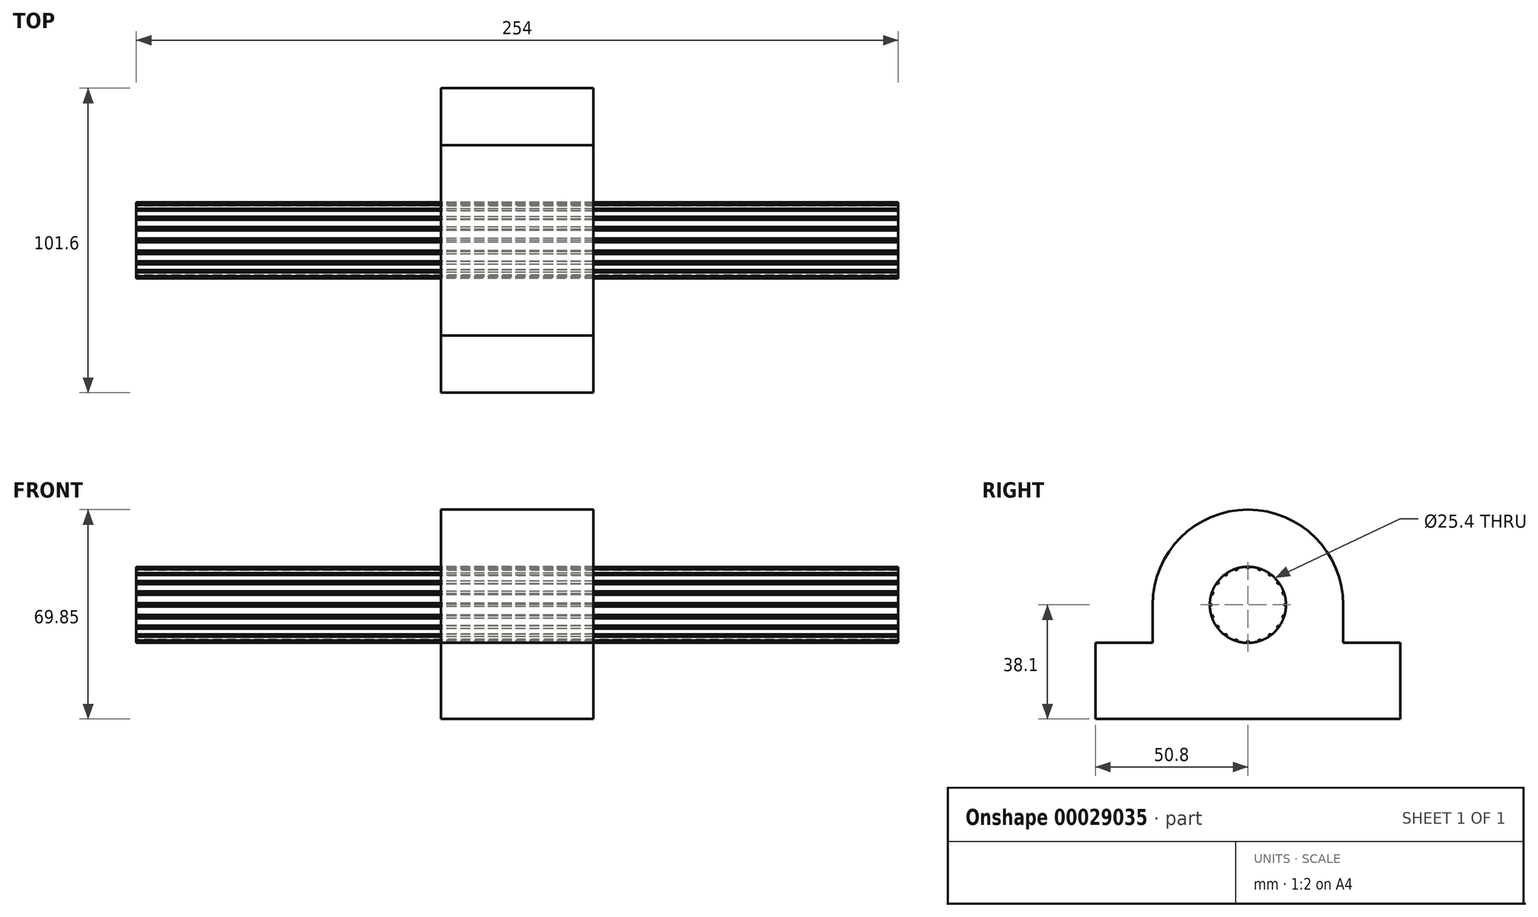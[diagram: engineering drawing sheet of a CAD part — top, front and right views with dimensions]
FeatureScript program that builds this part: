
annotation { "Feature Type Name" : "Feature", "Feature Type Description" : "" }
export const myFeature = defineFeature(function(context is Context, id is Id, definition is map)
    precondition{}
    {
        {
            var Q0;
            Q0=qCreatedBy(makeId("Right.planeOp"),FACE);
            var sketch = newSketch(context, id + "F0", { "sketchPlane" : qUnion([Q0])});
            skArc(sketch, "E0", {"start": v(-0.62, 12.68) * mm, "mid": v(-1.99, 12.54) * mm, "end": v(-3.33, 12.26) * mm});
            skLineSegment(sketch, "E1", {"start": v(-0.62, 12.68) * mm, "end": v(0, 12.06) * mm});
            skLineSegment(sketch, "E2", {"start": v(0, 12.06) * mm, "end": v(0.62, 12.68) * mm});
            skCircle(sketch, "E3", {"center": v(0, 0) * mm, "radius": 12.07 * mm, "construction": true});
            skLineSegment(sketch, "E4.1.0", {"start": v(-4.5, 11.87) * mm, "end": v(-3.73, 11.47) * mm});
            skLineSegment(sketch, "E4.1.1", {"start": v(-3.73, 11.47) * mm, "end": v(-3.33, 12.26) * mm});
            skLineSegment(sketch, "E4.2.0", {"start": v(-7.96, 9.9) * mm, "end": v(-7.1, 9.76) * mm});
            skLineSegment(sketch, "E4.2.1", {"start": v(-7.1, 9.76) * mm, "end": v(-6.95, 10.63) * mm});
            skLineSegment(sketch, "E4.3.0", {"start": v(-10.63, 6.95) * mm, "end": v(-9.76, 7.1) * mm});
            skLineSegment(sketch, "E4.3.1", {"start": v(-9.76, 7.1) * mm, "end": v(-9.9, 7.96) * mm});
            skLineSegment(sketch, "E4.4.0", {"start": v(-12.26, 3.33) * mm, "end": v(-11.47, 3.73) * mm});
            skLineSegment(sketch, "E4.4.1", {"start": v(-11.47, 3.73) * mm, "end": v(-11.87, 4.5) * mm});
            skLineSegment(sketch, "E4.5.0", {"start": v(-12.68, -0.62) * mm, "end": v(-12.06, 0) * mm});
            skLineSegment(sketch, "E4.5.1", {"start": v(-12.06, 0) * mm, "end": v(-12.68, 0.62) * mm});
            skLineSegment(sketch, "E4.6.0", {"start": v(-11.87, -4.5) * mm, "end": v(-11.47, -3.73) * mm});
            skLineSegment(sketch, "E4.6.1", {"start": v(-11.47, -3.73) * mm, "end": v(-12.26, -3.33) * mm});
            skLineSegment(sketch, "E4.7.0", {"start": v(-9.9, -7.96) * mm, "end": v(-9.76, -7.1) * mm});
            skLineSegment(sketch, "E4.7.1", {"start": v(-9.76, -7.1) * mm, "end": v(-10.63, -6.95) * mm});
            skLineSegment(sketch, "E4.8.0", {"start": v(-6.95, -10.63) * mm, "end": v(-7.1, -9.76) * mm});
            skLineSegment(sketch, "E4.8.1", {"start": v(-7.1, -9.76) * mm, "end": v(-7.96, -9.9) * mm});
            skLineSegment(sketch, "E4.9.0", {"start": v(-3.33, -12.26) * mm, "end": v(-3.73, -11.47) * mm});
            skLineSegment(sketch, "E4.9.1", {"start": v(-3.73, -11.47) * mm, "end": v(-4.5, -11.87) * mm});
            skLineSegment(sketch, "E4.10.0", {"start": v(0.62, -12.68) * mm, "end": v(0, -12.06) * mm});
            skLineSegment(sketch, "E4.10.1", {"start": v(0, -12.06) * mm, "end": v(-0.62, -12.68) * mm});
            skLineSegment(sketch, "E4.11.0", {"start": v(4.5, -11.87) * mm, "end": v(3.73, -11.47) * mm});
            skLineSegment(sketch, "E4.11.1", {"start": v(3.73, -11.47) * mm, "end": v(3.33, -12.26) * mm});
            skLineSegment(sketch, "E4.12.0", {"start": v(7.96, -9.9) * mm, "end": v(7.1, -9.76) * mm});
            skLineSegment(sketch, "E4.12.1", {"start": v(7.1, -9.76) * mm, "end": v(6.95, -10.63) * mm});
            skLineSegment(sketch, "E4.13.0", {"start": v(10.63, -6.95) * mm, "end": v(9.76, -7.1) * mm});
            skLineSegment(sketch, "E4.13.1", {"start": v(9.76, -7.1) * mm, "end": v(9.9, -7.96) * mm});
            skLineSegment(sketch, "E4.14.0", {"start": v(12.26, -3.33) * mm, "end": v(11.47, -3.73) * mm});
            skLineSegment(sketch, "E4.14.1", {"start": v(11.47, -3.73) * mm, "end": v(11.87, -4.5) * mm});
            skLineSegment(sketch, "E4.15.0", {"start": v(12.68, 0.62) * mm, "end": v(12.06, 0) * mm});
            skLineSegment(sketch, "E4.15.1", {"start": v(12.06, 0) * mm, "end": v(12.68, -0.62) * mm});
            skLineSegment(sketch, "E4.16.0", {"start": v(11.87, 4.5) * mm, "end": v(11.47, 3.73) * mm});
            skLineSegment(sketch, "E4.16.1", {"start": v(11.47, 3.73) * mm, "end": v(12.26, 3.33) * mm});
            skLineSegment(sketch, "E4.17.0", {"start": v(9.9, 7.96) * mm, "end": v(9.76, 7.1) * mm});
            skLineSegment(sketch, "E4.17.1", {"start": v(9.76, 7.1) * mm, "end": v(10.63, 6.95) * mm});
            skLineSegment(sketch, "E4.18.0", {"start": v(6.95, 10.63) * mm, "end": v(7.1, 9.76) * mm});
            skLineSegment(sketch, "E4.18.1", {"start": v(7.1, 9.76) * mm, "end": v(7.96, 9.9) * mm});
            skLineSegment(sketch, "E4.19.0", {"start": v(3.33, 12.26) * mm, "end": v(3.73, 11.47) * mm});
            skLineSegment(sketch, "E4.19.1", {"start": v(3.73, 11.47) * mm, "end": v(4.5, 11.87) * mm});
            skArc(sketch, "E5.trimOffspring", {"start": v(3.33, 12.26) * mm, "mid": v(1.99, 12.54) * mm, "end": v(0.62, 12.68) * mm});
            skArc(sketch, "E6.trimOffspring", {"start": v(6.95, 10.63) * mm, "mid": v(5.77, 11.32) * mm, "end": v(4.5, 11.87) * mm});
            skArc(sketch, "E7.trimOffspring", {"start": v(9.9, 7.96) * mm, "mid": v(8.98, 8.98) * mm, "end": v(7.96, 9.9) * mm});
            skArc(sketch, "E8.trimOffspring", {"start": v(11.87, 4.5) * mm, "mid": v(11.32, 5.77) * mm, "end": v(10.63, 6.95) * mm});
            skArc(sketch, "E9.trimOffspring", {"start": v(12.68, 0.62) * mm, "mid": v(12.54, 1.99) * mm, "end": v(12.26, 3.33) * mm});
            skArc(sketch, "E10.trimOffspring", {"start": v(12.26, -3.33) * mm, "mid": v(12.54, -1.99) * mm, "end": v(12.68, -0.62) * mm});
            skArc(sketch, "E11.trimOffspring", {"start": v(10.63, -6.95) * mm, "mid": v(11.32, -5.77) * mm, "end": v(11.87, -4.5) * mm});
            skArc(sketch, "E12.trimOffspring", {"start": v(7.96, -9.9) * mm, "mid": v(8.98, -8.98) * mm, "end": v(9.9, -7.96) * mm});
            skArc(sketch, "E13.trimOffspring", {"start": v(4.5, -11.87) * mm, "mid": v(5.77, -11.32) * mm, "end": v(6.95, -10.63) * mm});
            skArc(sketch, "E14.trimOffspring", {"start": v(0.62, -12.68) * mm, "mid": v(1.99, -12.54) * mm, "end": v(3.33, -12.26) * mm});
            skArc(sketch, "E15.trimOffspring", {"start": v(-3.33, -12.26) * mm, "mid": v(-1.99, -12.54) * mm, "end": v(-0.62, -12.68) * mm});
            skArc(sketch, "E16.trimOffspring", {"start": v(-6.95, -10.63) * mm, "mid": v(-5.77, -11.32) * mm, "end": v(-4.5, -11.87) * mm});
            skArc(sketch, "E17.trimOffspring", {"start": v(-9.9, -7.96) * mm, "mid": v(-8.98, -8.98) * mm, "end": v(-7.96, -9.9) * mm});
            skArc(sketch, "E18.trimOffspring", {"start": v(-11.87, -4.5) * mm, "mid": v(-11.32, -5.77) * mm, "end": v(-10.63, -6.95) * mm});
            skArc(sketch, "E19.trimOffspring", {"start": v(-12.68, -0.62) * mm, "mid": v(-12.54, -1.99) * mm, "end": v(-12.26, -3.33) * mm});
            skArc(sketch, "E20.trimOffspring", {"start": v(-12.26, 3.33) * mm, "mid": v(-12.54, 1.99) * mm, "end": v(-12.68, 0.62) * mm});
            skArc(sketch, "E21.trimOffspring", {"start": v(-10.63, 6.95) * mm, "mid": v(-11.32, 5.77) * mm, "end": v(-11.87, 4.5) * mm});
            skArc(sketch, "E22.trimOffspring", {"start": v(-7.96, 9.9) * mm, "mid": v(-8.98, 8.98) * mm, "end": v(-9.9, 7.96) * mm});
            skArc(sketch, "E23.trimOffspring", {"start": v(-4.5, 11.87) * mm, "mid": v(-5.77, 11.32) * mm, "end": v(-6.95, 10.63) * mm});
            skSolve(sketch);
        }
        {
            var Q0;
            Q0=makeQuery(id+"F0.imprint","IMPRINT",FACE,{"disambiguationData":[TD([[makeQuery(id+"F0.imprint","IMPRINT",EDGE,{"derivedFrom":sQuery(id+"F0.wireOp",EDGE,"E0")}),1.0]])]});
            extrude(context, id + "F1", {"entities" : qUnion([Q0]), "endBound" : BoundingType.SYMMETRIC, "depth" : 254 * mm});
        }
        {
            var Q0;
            Q0=qCreatedBy(makeId("Right.planeOp"),FACE);
            var sketch = newSketch(context, id + "F2", { "sketchPlane" : qUnion([Q0])});
            skCircle(sketch, "E24", {"center": v(0, 0) * mm, "radius": 12.7 * mm});
            skArc(sketch, "E25", {"start": v(31.75, 0) * mm, "mid": v(0, 31.75) * mm, "end": v(-31.75, 0) * mm});
            skLineSegment(sketch, "E26.rect.bottom", {"start": v(50.8, -12.7) * mm, "end": v(31.75, -12.7) * mm});
            skLineSegment(sketch, "E26.rect.top", {"start": v(50.8, -38.1) * mm, "end": v(-50.8, -38.1) * mm});
            skLineSegment(sketch, "E26.rect.left", {"start": v(50.8, -12.7) * mm, "end": v(50.8, -38.1) * mm});
            skLineSegment(sketch, "E26.rect.right", {"start": v(-50.8, -12.7) * mm, "end": v(-50.8, -38.1) * mm});
            skPoint(sketch, "E26.rect.middle", {"position": v(0, -25.4) * mm});
            skLineSegment(sketch, "E27", {"start": v(-31.75, 0) * mm, "end": v(-31.75, -12.7) * mm});
            skLineSegment(sketch, "E28", {"start": v(31.75, 0) * mm, "end": v(31.75, -12.7) * mm});
            skLineSegment(sketch, "E29.trimOffspring", {"start": v(-31.75, -12.7) * mm, "end": v(-50.8, -12.7) * mm});
            skSolve(sketch);
        }
        {
            var Q0;
            Q0=makeQuery(id+"F2.imprint","IMPRINT",FACE,{"disambiguationData":[TD([[makeQuery(id+"F2.imprint","IMPRINT",EDGE,{"derivedFrom":sQuery(id+"F2.wireOp",EDGE,"E24")}),-1.0]])]});
            extrude(context, id + "F3", {"entities" : qUnion([Q0]), "endBound" : BoundingType.SYMMETRIC, "depth" : 50.8 * mm});
        }
    });
